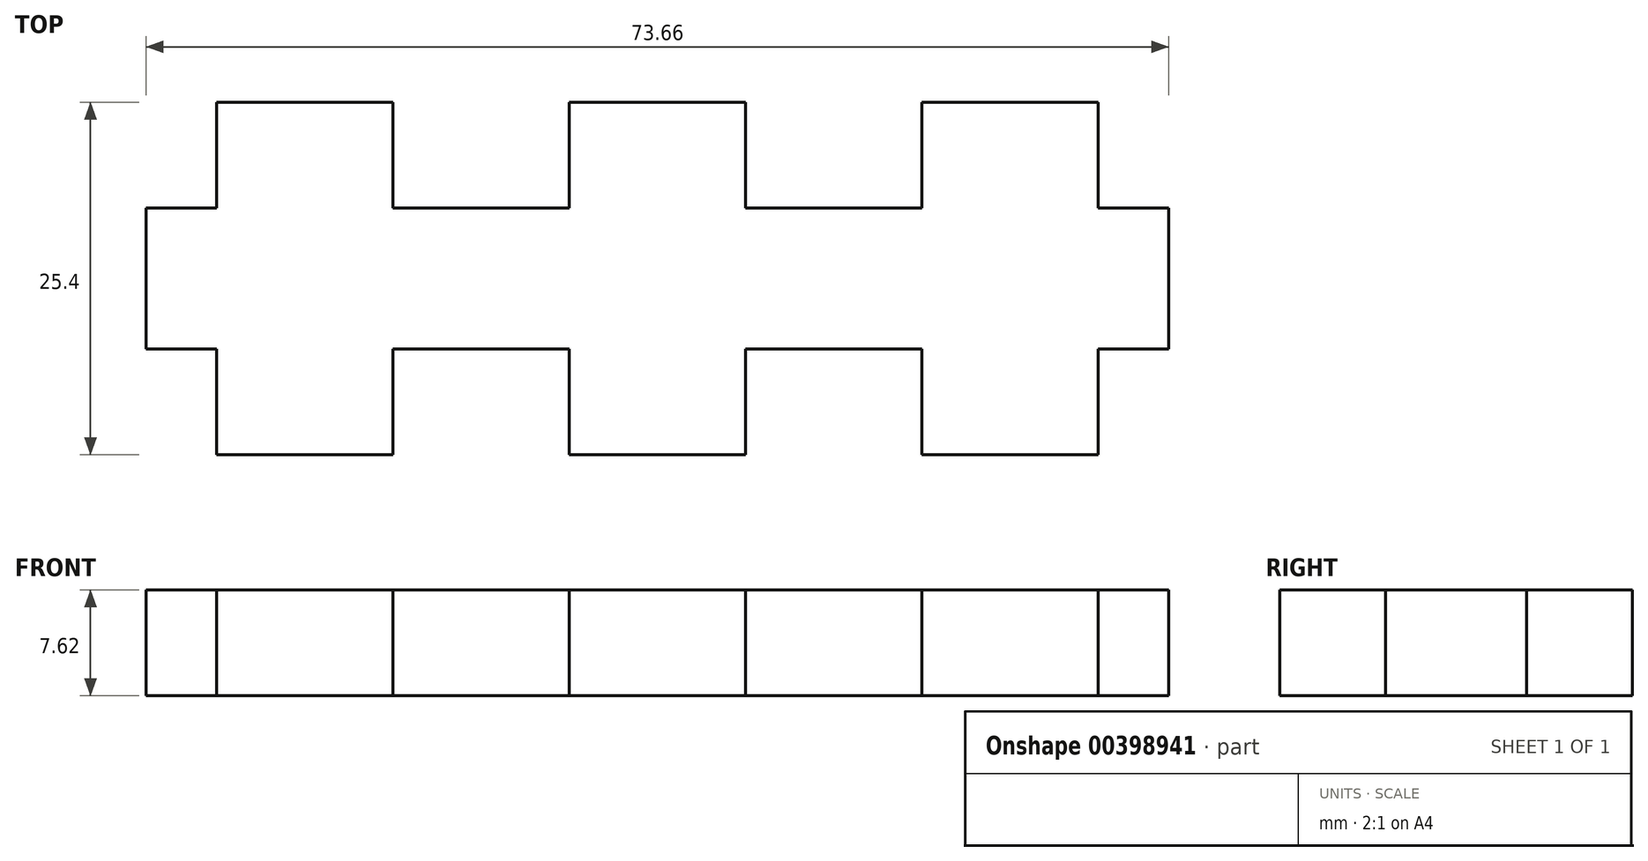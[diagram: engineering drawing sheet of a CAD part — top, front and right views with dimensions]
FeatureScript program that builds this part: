
annotation { "Feature Type Name" : "Feature", "Feature Type Description" : "" }
export const myFeature = defineFeature(function(context is Context, id is Id, definition is map)
    precondition{}
    {
        {
            var Q0;
            Q0=qCreatedBy(makeId("Top.planeOp"),FACE);
            var sketch = newSketch(context, id + "F0", { "sketchPlane" : qUnion([Q0])});
            skLineSegment(sketch, "E0.bottom", {"start": v(5.08, 0) * mm, "end": v(17.78, 0) * mm});
            skLineSegment(sketch, "E1", {"start": v(0, -7.62) * mm, "end": v(5.08, -7.62) * mm});
            skLineSegment(sketch, "E2", {"start": v(5.08, -7.62) * mm, "end": v(5.08, 0) * mm});
            skLineSegment(sketch, "E3", {"start": v(17.78, 0) * mm, "end": v(17.78, -7.62) * mm});
            skLineSegment(sketch, "E4", {"start": v(17.78, -7.62) * mm, "end": v(30.48, -7.62) * mm});
            skLineSegment(sketch, "E5", {"start": v(30.48, -7.62) * mm, "end": v(30.48, 0) * mm});
            skLineSegment(sketch, "E6", {"start": v(30.48, 0) * mm, "end": v(43.18, 0) * mm});
            skLineSegment(sketch, "E7", {"start": v(43.18, 0) * mm, "end": v(43.18, -7.62) * mm});
            skLineSegment(sketch, "E8", {"start": v(43.18, -7.62) * mm, "end": v(55.88, -7.62) * mm});
            skLineSegment(sketch, "E9", {"start": v(55.88, -7.62) * mm, "end": v(55.88, 0) * mm});
            skLineSegment(sketch, "E10", {"start": v(55.88, 0) * mm, "end": v(68.58, 0) * mm});
            skLineSegment(sketch, "E11", {"start": v(68.58, 0) * mm, "end": v(68.58, -7.62) * mm});
            skPoint(sketch, "E12.orphan", {"position": v(88.9, 0) * mm});
            skPoint(sketch, "E13.orphan", {"position": v(0, 0) * mm});
            skLineSegment(sketch, "E14", {"start": v(0, -17.78) * mm, "end": v(5.08, -17.78) * mm});
            skLineSegment(sketch, "E15", {"start": v(5.08, -17.78) * mm, "end": v(5.08, -25.4) * mm});
            skLineSegment(sketch, "E16", {"start": v(5.08, -25.4) * mm, "end": v(17.78, -25.4) * mm});
            skLineSegment(sketch, "E17", {"start": v(17.78, -25.4) * mm, "end": v(17.78, -17.78) * mm});
            skLineSegment(sketch, "E18", {"start": v(17.78, -17.78) * mm, "end": v(30.48, -17.78) * mm});
            skLineSegment(sketch, "E19", {"start": v(30.48, -17.78) * mm, "end": v(30.48, -25.4) * mm});
            skLineSegment(sketch, "E20", {"start": v(30.48, -25.4) * mm, "end": v(43.18, -25.4) * mm});
            skLineSegment(sketch, "E21", {"start": v(43.18, -25.4) * mm, "end": v(43.18, -17.78) * mm});
            skLineSegment(sketch, "E22", {"start": v(43.18, -17.78) * mm, "end": v(55.88, -17.78) * mm});
            skLineSegment(sketch, "E23", {"start": v(55.88, -17.78) * mm, "end": v(55.88, -25.4) * mm});
            skLineSegment(sketch, "E24", {"start": v(55.88, -25.4) * mm, "end": v(68.58, -25.4) * mm});
            skLineSegment(sketch, "E25", {"start": v(68.58, -25.4) * mm, "end": v(68.58, -17.78) * mm});
            skPoint(sketch, "E26.orphan", {"position": v(0, -25.4) * mm});
            skLineSegment(sketch, "E27", {"start": v(0, -7.62) * mm, "end": v(0, -17.78) * mm});
            skLineSegment(sketch, "E28", {"start": v(36.83, 0) * mm, "end": v(36.83, -15.2) * mm, "construction": true});
            skLineSegment(sketch, "E29.MirrorCS", {"start": v(73.66, -7.62) * mm, "end": v(68.58, -7.62) * mm});
            skLineSegment(sketch, "E30.MirrorCS", {"start": v(73.66, -7.62) * mm, "end": v(73.66, -17.78) * mm});
            skLineSegment(sketch, "E31.MirrorCS", {"start": v(73.66, -17.78) * mm, "end": v(68.58, -17.78) * mm});
            skLineSegment(sketch, "E32", {"start": v(0, 0) * mm, "end": v(5.08, 0) * mm, "construction": true});
            skLineSegment(sketch, "E33", {"start": v(0, 0) * mm, "end": v(0, -7.62) * mm, "construction": true});
            skSolve(sketch);
        }
        {
            var Q0;
            Q0=makeQuery(id+"F0.imprint","IMPRINT",FACE,{"disambiguationData":[TD([[makeQuery(id+"F0.imprint","IMPRINT",EDGE,{"derivedFrom":sQuery(id+"F0.wireOp",EDGE,"E1")}),-1.0]])]});
            extrude(context, id + "F1", {"entities" : qUnion([Q0]), "depth" : 7.62 * mm, "offsetDistance" : 25.4 * mm});
        }
    });
